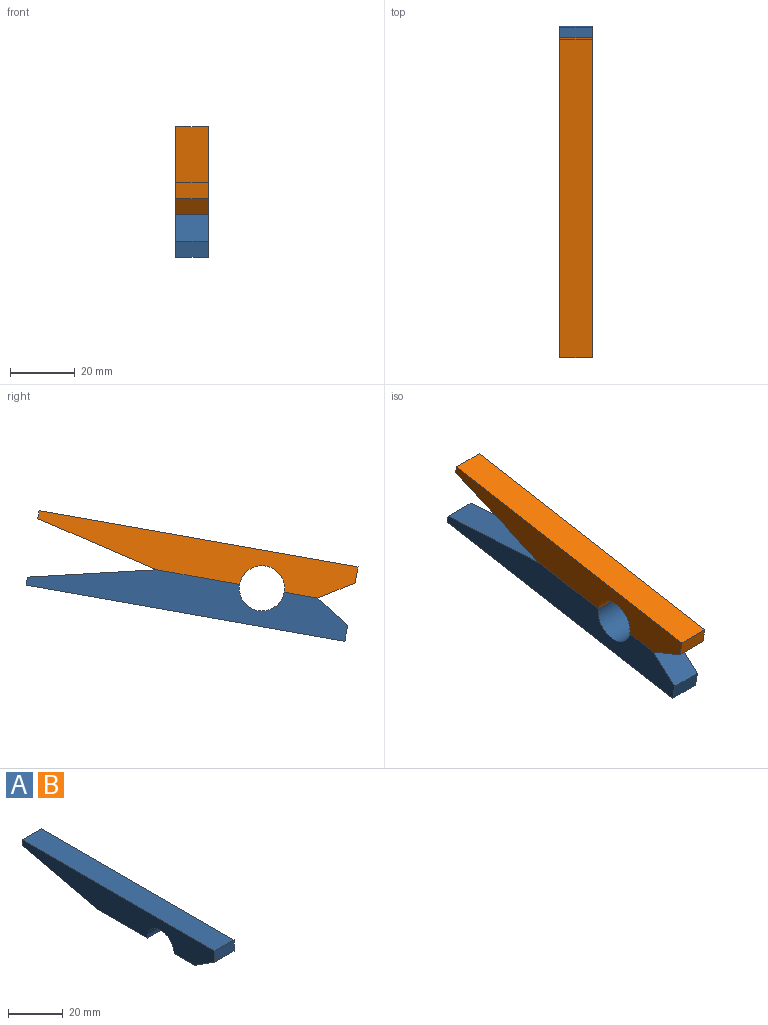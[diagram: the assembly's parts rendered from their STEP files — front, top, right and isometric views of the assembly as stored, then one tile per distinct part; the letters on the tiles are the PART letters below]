
ASSEMBLY  parts=2 mates=1
PART A: 10 faces, bbox 10x100x11.7 mm
  f0: plane 10.5x10mm, normal (0,0,-1), area 105mm2, adj f1,f7,f8,f9
  f1: cylinder r=7mm len=14mm, axis (-1,0,0), area 219.9mm2, adj f0,f2,f8,f9
  f2: plane 26x10mm, normal (0,0,-1), area 260mm2, adj f1,f3,f8,f9
  f3: plane 38.93x10mm, normal (0,0.23,-0.97), area 400mm2, adj f2,f4,f8,f9
  f4: plane 10x2.5mm, normal (0,1,0), area 25mm2, adj f3,f5,f8,f9
  f5: plane 100x10mm, normal (0,0,1), area 1000mm2, adj f4,f6,f8,f9
  f6: plane 10x5mm, normal (0,-1,0), area 50mm2, adj f5,f7,f8,f9
  f7: plane 10.57x10mm, normal (0,-0.53,-0.85), area 125mm2, adj f0,f6,f8,f9
  f8: plane 100x11.68mm, normal (1,0,0), area 876.8mm2, adj f0,f1,f2,f3,f4,f5,f6,f7
  f9: plane 100x11.68mm, normal (-1,0,0), area 876.8mm2, adj f0,f1,f2,f3,f4,f5,f6,f7
PART B: same geometry as A
PLACE A rot(axis=(0,-1,-0.09),180deg) t=(-5,2.93,-8.9)mm fixed
PLACE B rot(axis=(1,0,0),10deg) t=(-5,2.93,-8.9)mm
MATE revolute A.f9 <-> B.f8  axis (1,0,0) through (0,15.52,-6.68)mm
